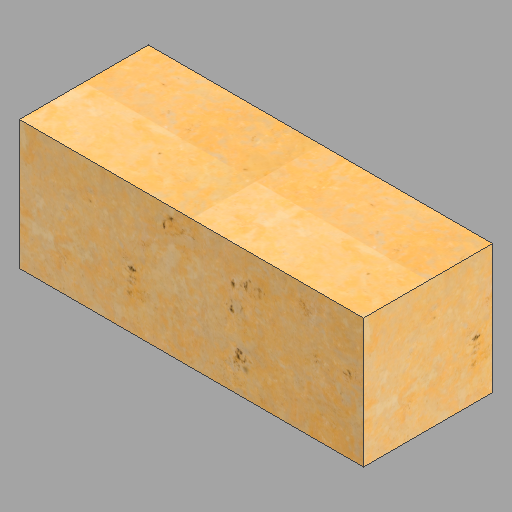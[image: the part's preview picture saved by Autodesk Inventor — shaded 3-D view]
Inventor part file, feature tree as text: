
AUTODESK INVENTOR PART (.ipt)
format: ipt  version: 2023 (Build 270158030, 158C)  size: 353,792 bytes
history: native  units: in
note: dims shown in document units (in); Inventor stores cm internally (conversion verified against a paired STEP export)
features: other x1, extrude x1, sketch x1
ambient origin geometry x8: Origin, YZ Plane, XZ Plane, XY Plane, X Axis, Y Axis, Z Axis, Center Point
bodies: Solid1 (feature_tree)
feature tree (3):
  other  "Bench Typ1 - 4"
  extrude  "Extrusion1"  Depth=18.0in
  sketch  "Sketch1"  dims[d0=48.0in d1=18.0in d2=18.0in d3=0.0in]
